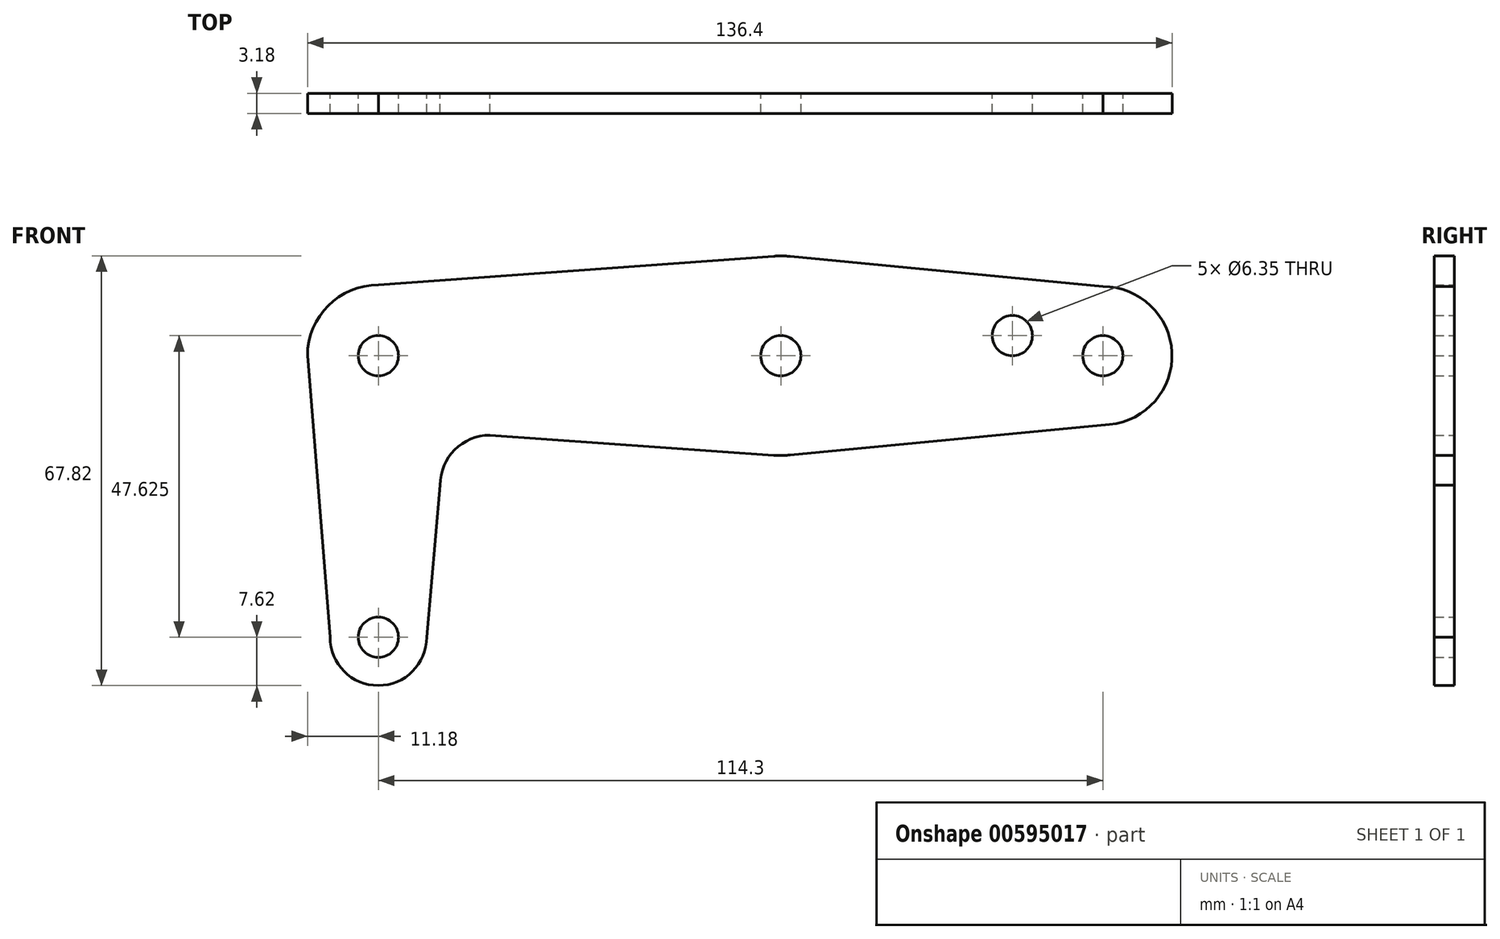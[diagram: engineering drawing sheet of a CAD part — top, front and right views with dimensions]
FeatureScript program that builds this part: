
annotation { "Feature Type Name" : "Feature", "Feature Type Description" : "" }
export const myFeature = defineFeature(function(context is Context, id is Id, definition is map)
    precondition{}
    {
        {
            var Q0;
            Q0=qCreatedBy(makeId("Front.planeOp"),FACE);
            var sketch = newSketch(context, id + "F0", { "sketchPlane" : qUnion([Q0])});
            skLineSegment(sketch, "E0", {"start": v(-102.39, 0) * mm, "end": v(92.32, 0) * mm, "construction": true});
            skLineSegment(sketch, "E1", {"start": v(0, 31.6) * mm, "end": v(0, -24.8) * mm, "construction": true});
            skLineSegment(sketch, "E2", {"start": v(-74.68, 0) * mm, "end": v(-71.12, -44.45) * mm});
            skArc(sketch, "E3", {"start": v(-63.5, 11.18) * mm, "mid": v(-71.4, 7.9) * mm, "end": v(-74.68, 0) * mm});
            skLineSegment(sketch, "E4", {"start": v(-63.5, 11.18) * mm, "end": v(-1.14, 15.7) * mm});
            skLineSegment(sketch, "E5", {"start": v(1.51, 15.68) * mm, "end": v(50.8, 10.92) * mm});
            skCircle(sketch, "E6", {"center": v(50.8, 0) * mm, "radius": 3.17 * mm});
            skCircle(sketch, "E7", {"center": v(0, 0) * mm, "radius": 3.18 * mm});
            skCircle(sketch, "E8", {"center": v(-63.5, 0) * mm, "radius": 3.18 * mm});
            skLineSegment(sketch, "E9", {"start": v(-63.5, 0) * mm, "end": v(-63.5, -66.8) * mm, "construction": true});
            skArc(sketch, "E10", {"start": v(-71.12, -44.45) * mm, "mid": v(-63.5, -52.07) * mm, "end": v(-55.88, -44.45) * mm});
            skLineSegment(sketch, "E11", {"start": v(-55.88, -44.45) * mm, "end": v(-53.75, -20.42) * mm});
            skArc(sketch, "E12", {"start": v(-45.87, -12.55) * mm, "mid": v(-51.44, -14.85) * mm, "end": v(-53.75, -20.42) * mm});
            skLineSegment(sketch, "E13", {"start": v(-45.87, -12.55) * mm, "end": v(-1.1, -15.7) * mm});
            skLineSegment(sketch, "E14", {"start": v(1.5, -15.68) * mm, "end": v(51.84, -10.87) * mm});
            skArc(sketch, "E15", {"start": v(51.84, -10.87) * mm, "mid": v(61.7, 0.52) * mm, "end": v(50.8, 10.92) * mm});
            skPoint(sketch, "E16.visualSharp", {"position": v(0.2, -15.8) * mm});
            skArc(sketch, "E16.filletArc", {"start": v(-1.1, -15.7) * mm, "mid": v(0.2, -15.75) * mm, "end": v(1.5, -15.68) * mm});
            skCircle(sketch, "E17", {"center": v(-63.5, -44.45) * mm, "radius": 3.18 * mm});
            skPoint(sketch, "E18.visualSharp", {"position": v(0, 15.82) * mm});
            skArc(sketch, "E18.filletArc", {"start": v(1.51, 15.68) * mm, "mid": v(0.19, 15.75) * mm, "end": v(-1.14, 15.7) * mm});
            skCircle(sketch, "E19", {"center": v(36.53, 3.18) * mm, "radius": 3.18 * mm});
            skSolve(sketch);
        }
        {
            var Q0;
            Q0 = qSketchRegion(id + "F0", true);
            extrude(context, id + "F1", {"entities" : qUnion([Q0]), "depth" : 3.17 * mm, "offsetDistance" : 25.4 * mm});
        }
    });
